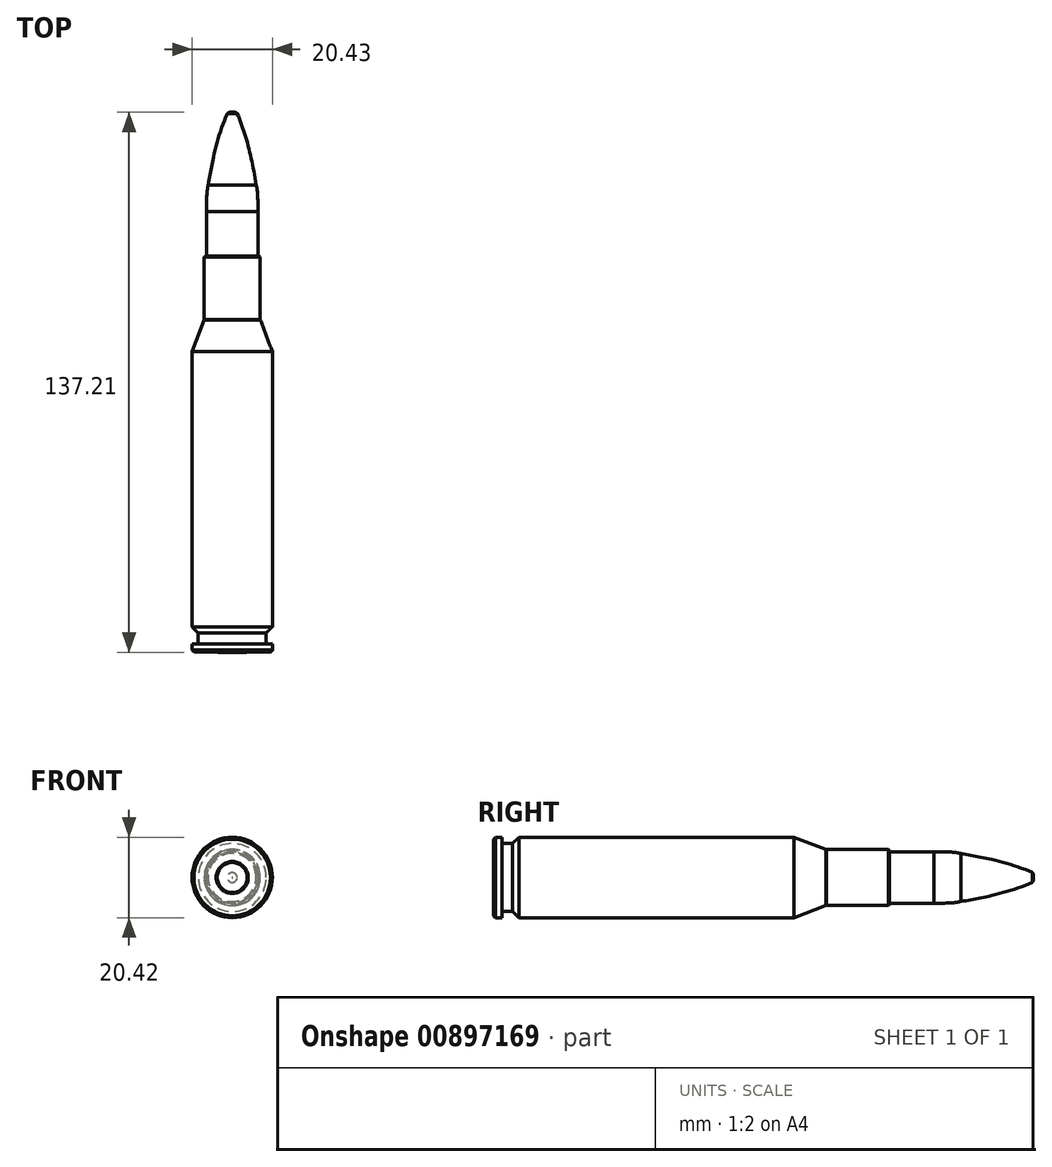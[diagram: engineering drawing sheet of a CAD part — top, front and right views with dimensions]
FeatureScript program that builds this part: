
annotation { "Feature Type Name" : "Feature", "Feature Type Description" : "" }
export const myFeature = defineFeature(function(context is Context, id is Id, definition is map)
    precondition{}
    {
        {
            var Q0;
            Q0=qCreatedBy(makeId("Top.planeOp"),FACE);
            var sketch = newSketch(context, id + "F0", { "sketchPlane" : qUnion([Q0])});
            skLineSegment(sketch, "E0", {"start": v(-15.33, -69.1) * mm, "end": v(-19.13, -69.1) * mm});
            skLineSegment(sketch, "E1", {"start": v(-19.13, -69.1) * mm, "end": v(-19.13, -74.49) * mm});
            skLineSegment(sketch, "E2", {"start": v(-15.33, -74.45) * mm, "end": v(-25.54, -74.45) * mm});
            skLineSegment(sketch, "E3", {"start": v(-25.54, -74.45) * mm, "end": v(-25.54, -72.34) * mm});
            skLineSegment(sketch, "E4", {"start": v(-25.54, -72.34) * mm, "end": v(-23.96, -72.34) * mm});
            skLineSegment(sketch, "E5", {"start": v(-23.96, -72.34) * mm, "end": v(-23.96, -69.58) * mm});
            skLineSegment(sketch, "E6", {"start": v(-23.96, -69.58) * mm, "end": v(-25.54, -68) * mm});
            skLineSegment(sketch, "E7", {"start": v(-25.54, -68) * mm, "end": v(-25.54, 1.9) * mm});
            skLineSegment(sketch, "E8", {"start": v(-22.44, 10.04) * mm, "end": v(-22.44, 26.14) * mm});
            skLineSegment(sketch, "E9", {"start": v(-25.54, -68) * mm, "end": v(-25.54, -70.26) * mm});
            skLineSegment(sketch, "E10", {"start": v(-25.54, 1.9) * mm, "end": v(-22.44, 10.04) * mm});
            skLineSegment(sketch, "E11", {"start": v(-22.44, 26.14) * mm, "end": v(-21.45, 26.14) * mm});
            skLineSegment(sketch, "E12", {"start": v(-15.36, 37.48) * mm, "end": v(-21.85, 37.48) * mm});
            skLineSegment(sketch, "E13", {"start": v(-21.85, 37.48) * mm, "end": v(-21.85, 26.82) * mm});
            skFitSpline(sketch, "E14", {"points": [v(-21.85, 26.82) * mm, v(-21.45, 26.14) * mm], "startDerivative": vector(0, -1.61) * mm, "endDerivative": vector(1.49, 0) * mm});
            skFitSpline(sketch, "E15", {"points": [v(-21.85, 37.48) * mm, v(-21.44, 44.27) * mm], "startDerivative": vector(-0.07, 5.87) * mm, "endDerivative": vector(1.37, 5.74) * mm});
            skLineSegment(sketch, "E16", {"start": v(-15.33, 62.7) * mm, "end": v(-15.33, 26.14) * mm});
            skLineSegment(sketch, "E17", {"start": v(-15.33, -74.45) * mm, "end": v(-15.33, 26.14) * mm});
            skLineSegment(sketch, "E18", {"start": v(-21.45, 26.14) * mm, "end": v(-15.33, 26.14) * mm});
            skLineSegment(sketch, "E19", {"start": v(-15.33, 62.7) * mm, "end": v(-15.39, 62.7) * mm});
            skFitSpline(sketch, "E20", {"points": [v(-15.39, 62.7) * mm, v(-16.57, 62.44) * mm], "startDerivative": vector(-2.53, 0.23) * mm, "endDerivative": vector(-0.47, -0.42) * mm});
            skFitSpline(sketch, "E21", {"points": [v(-16.57, 62.44) * mm, v(-21.44, 44.27) * mm], "startDerivative": vector(-7.34, -16.65) * mm, "endDerivative": vector(-3.47, -20.14) * mm});
            skSolve(sketch);
        }
        {
            var Q0;
            {var subQ0=sQuery(id+"F0.wireOp",EDGE,"E0");Q0=makeQuery(id+"F0.imprint","IMPRINT",FACE,{"disambiguationData":[TD([[makeQuery(id+"F0.imprint","IMPRINT",EDGE,{"derivedFrom":subQ0}),-1.0]])]});}
            var Q1;
            {var subQ1=sQuery(id+"F0.wireOp",EDGE,"E12");Q1=makeQuery(id+"F0.imprint","IMPRINT",FACE,{"disambiguationData":[TD([[makeQuery(id+"F0.imprint","IMPRINT",EDGE,{"derivedFrom":subQ1}),1.0]])]});}
            var Q2;
            {var subQ1=sQuery(id+"F0.wireOp",EDGE,"E12");Q2=makeQuery(id+"F0.imprint","IMPRINT",FACE,{"disambiguationData":[TD([[makeQuery(id+"F0.imprint","IMPRINT",EDGE,{"derivedFrom":subQ1}),-1.0]])]});}
            var Q3;
            Q3=makeQuery(id+"F0.imprint","IMPRINT",FACE,{"disambiguationData":[TD([[makeQuery(id+"F0.imprint","IMPRINT",EDGE,{"derivedFrom":sQuery(id+"F0.wireOp",EDGE,"E13")}),1.0]])]});
            var Q4;
            Q4=sQuery(id+"F0.wireOp",EDGE,"E17");
            revolve(context, id + "F1", {"surfaceOperationType" : NewSurfaceOperationType.NEW, "entities" : qUnion([Q0, Q1, Q2, Q3]), "axis" : qUnion([Q4]), "revolveType" : RevolveType.FULL});
        }
        {
            var Q0;
            Q0=makeQuery(id+"F1.opRevolve","SWEPT_EDGE",EDGE,{"disambiguationData":[OSD([sQuery(id+"F0.wireOp",EDGE,"E1"),sQuery(id+"F0.wireOp",EDGE,"E2")])]});
            var Q1;
            Q1=makeQuery(id+"F1.opRevolve","SWEPT_EDGE",EDGE,{"disambiguationData":[OSD([sQuery(id+"F0.wireOp",EDGE,"E8"),sQuery(id+"F0.wireOp",EDGE,"88vX6Dcv-yaL2-YR9K-8U8G-9htzLIJxvQV1")])]});
            chamfer(context, id + "F2", {"entities" : qUnion([Q0, Q1]), "width" : 0.25 * mm, "tangentPropagation" : true});
        }
        {
            var Q0;
            Q0=makeQuery(id+"F1.opRevolve","SWEPT_FACE",FACE,{"disambiguationData":[OSD([sQuery(id+"F0.wireOp",EDGE,"E0")])]});
            extrude(context, id + "F3", {"entities" : qUnion([Q0]), "operationType" : NewBodyOperationType.ADD, "depth" : 5.38 * mm, "offsetDistance" : 25.4 * mm});
        }
        {
            var Q0;
            Q0=makeQuery(id+"F3.opExtrude","CAP_EDGE",EDGE,{"disambiguationData":[OSD([sQuery(id+"F0.wireOp",EDGE,"E0"),sQuery(id+"F0.wireOp",EDGE,"E1")])],"isStart":false});
            fillet(context, id + "F4", {"entities" : qUnion([Q0]), "radius" : 0.25 * mm, "tangentPropagation" : true, "allowEdgeOverflow" : false});
        }
        {
            var Q0;
            Q0=makeQuery(id+"F1.opRevolve","SWEPT_EDGE",EDGE,{"disambiguationData":[OSD([sQuery(id+"F0.wireOp",EDGE,"E2"),sQuery(id+"F0.wireOp",EDGE,"E3")])]});
            chamfer(context, id + "F5", {"entities" : qUnion([Q0]), "width" : 0.5 * mm, "tangentPropagation" : true});
        }
    });
